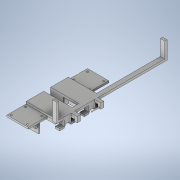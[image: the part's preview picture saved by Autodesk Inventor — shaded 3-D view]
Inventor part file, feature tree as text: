
AUTODESK INVENTOR PART (.ipt)
format: ipt  version: 2020.2 (Build 242310000, 310)  size: 848,896 bytes
history: native  units: mm
features: sketch x34, extrude x34, projected_geometry x17, hole x3
ambient origin geometry x8: Origin, YZ Plane, XZ Plane, XY Plane, X Axis, Y Axis, Z Axis, Center Point
bodies: Solid1 (feature_tree)
feature tree (88):
  sketch  "Sketch1"  dims[d0=8.0mm d1=98.298mm]
  extrude  "Extrusion1"  Depth=98.298mm
  extrude  "Extrusion2"  Depth=4.0mm
  extrude  "Extrusion3"  Depth=4.0mm TaperAngle=0.0deg
  extrude  "Extrusion4"  Depth=34.0mm
  extrude  "Extrusion5"  Depth=12.7mm
  extrude  "Extrusion6"  Depth=25.0mm
  hole  "Hole1"  [1 undecoded]
  extrude  "Extrusion11"  TaperAngle=60.0deg  [1 undecoded]
  extrude  "Extrusion12"  TaperAngle=120.0deg  [1 undecoded]
  sketch  "Sketch16"  dims[d19=6.4262mm d20=120.0deg]
  extrude  "Extrusion13"  Depth=6.4262mm
  extrude  "Extrusion14"  Depth=6.4262mm
  sketch  "Sketch17"  dims[d21=120.0deg d22=6.4262mm]
  extrude  "Extrusion15"  Depth=25.4mm TaperAngle=0.0deg
  extrude  "Extrusion18"  Depth=6.0mm
  extrude  "Extrusion19"  Depth=8.89mm
  extrude  "Extrusion20"  Depth=10.0mm
  hole  "Hole2"  [1 undecoded]
  extrude  "Extrusion21"  Depth=2.0mm
  extrude  "Extrusion22"  Depth=2.0mm
  sketch  "Sketch27"  dims[d45=8.89mm d46=2.0mm]
  extrude  "Extrusion23"  Depth=25.4mm
  extrude  "Extrusion24"  Depth=32.48mm
  extrude  "Extrusion25"  TaperAngle=90.0deg  [1 undecoded]
  sketch  "Sketch29"  dims[d79=51.53mm d80=32.48mm]
  extrude  "Extrusion26"  Depth=2.0mm
  extrude  "Extrusion27"  Depth=21.0mm
  extrude  "Extrusion28"  Depth=36.0mm TaperAngle=0.0deg
  extrude  "Extrusion29"  Depth=8.0mm
  extrude  "Extrusion30"  Depth=17.5mm
  extrude  "Extrusion32"  Depth=35.0mm
  extrude  "Extrusion38"  Depth=5.0mm
  extrude  "Extrusion39"  TaperAngle=90.0deg  [1 undecoded]
  extrude  "Extrusion40"  Depth=5.0mm
  hole  "Hole4"  [1 undecoded]
  extrude  "Extrusion43"  Depth=1.5mm
  extrude  "Extrusion44"  TaperAngle=0.0deg  [1 undecoded]
  extrude  "Extrusion45"  Depth=28.8036mm
  extrude  "Extrusion46"  Depth=25.4mm TaperAngle=0.0deg
  extrude  "Extrusion47"  Depth=2.0mm
  extrude  "Extrusion48"  Depth=2.0mm
  sketch  "Sketch2"  dims[d2=8.0mm d3=4.0mm]
  sketch  "Sketch3"  dims[d4=4.0mm d5=4.0mm d6=0.0mm]
  sketch  "Sketch4"  dims[d7=34.0mm d8=0.0mm d9=19.558mm]
  sketch  "Sketch5"  dims[d10=16.1125mm d11=12.7mm]
  sketch  "Sketch6"  dims[d12=25.0mm d13=0.0mm d14=11.1125mm]
  sketch  "Sketch14"  dims[d15=6.4135mm d16=12.827mm]
  projected_geometry  "Projected Loop2"
  sketch  "Sketch15"  dims[d17=6.4262mm d18=60.0deg]
  projected_geometry  "Projected Loop3"
  sketch  "Sketch18"  dims[d23=120.0deg d24=6.4262mm]
  sketch  "Sketch21"  dims[d25=120.0deg d26=25.4mm d27=0.0mm]
  sketch  "Sketch22"  dims[d28=6.0mm d29=8.89mm]
  sketch  "Sketch23"  dims[d30=5.9944mm d31=8.89mm]
  sketch  "Sketch24"  dims[d32=25.4mm d33=0.0mm d34=10.0mm]
  sketch  "Sketch25"  dims[d35=90.0deg d36=20.0mm]
  projected_geometry  "Projected Loop5"
  sketch  "Sketch26"  dims[d37=3.4mm d38=19.05mm d39=6.2992mm d40=6.35mm d41=90.0deg d42=5.0mm d43=0.0mm d44=2.0mm]
  sketch  "Sketch28"  dims[d47=25.4mm d48=0.0mm d78=16.24mm]
  sketch  "Sketch30"  dims[d81=90.0deg d82=90.0deg]
  sketch  "Sketch32"  dims[d83=4.0mm d84=0.0mm d87=2.0mm]
  projected_geometry  "Projected Loop6"
  sketch  "Sketch33"  dims[d88=2.0mm d89=21.0mm]
  projected_geometry  "Projected Loop7"
  sketch  "Sketch35"  dims[d90=2.0mm d91=36.0mm d92=0.0mm]
  projected_geometry  "Projected Loop8"
  sketch  "Sketch42"  dims[d93=13.878mm d94=8.0mm]
  sketch  "Sketch43"  dims[d95=180.0deg d96=17.5mm]
  projected_geometry  "Projected Loop9"
  projected_geometry  "Projected Loop10"
  projected_geometry  "Projected Loop11"
  projected_geometry  "Projected Loop12"
  sketch  "Sketch44"  dims[d97=90.0deg d98=35.0mm]
  sketch  "Sketch45"  dims[d99=3.5mm d100=5.0mm]
  sketch  "Sketch48"  dims[d101=7.0mm d102=90.0deg]
  sketch  "Sketch49"  dims[d103=5.0mm d104=3.4mm]
  projected_geometry  "Projected Loop13"
  projected_geometry  "Projected Loop14"
  sketch  "Sketch50"  dims[d105=3.4mm d106=25.4mm d107=0.0mm]
  projected_geometry  "Projected Loop15"
  sketch  "Sketch51"  dims[d108=6.4262mm d109=0.0mm d110=1.5mm]
  sketch  "Sketch52"  dims[d111=1.5mm d112=0.0mm d113=0.0mm]
  sketch  "Sketch53"  dims[d128=44.8mm d129=28.8036mm d130=25.4mm d131=0.0mm d132=3.2131mm d133=6.4262mm d134=120.0deg d135=3.2131mm d136=6.4262mm d137=120.0deg d138=25.4mm d139=0.0mm d140=8.001mm d141=13.8938mm d142=8.001mm d143=0.0mm d144=25.4mm d145=0.0mm d146=10.0mm d147=20.0mm d148=3.4mm d149=19.05mm d150=6.2992mm d151=6.35mm d152=90.0deg d153=5.0mm d154=0.0mm d155=16.2433mm d156=32.4866mm d157=51.5366mm d158=4.0mm d159=0.0mm d160=21.0mm d161=2.0mm d162=2.0mm d163=2.0mm d164=2.0mm d165=36.0mm d166=0.0mm d167=7.0mm d168=5.0mm d169=5.0mm d170=17.5mm d171=35.0mm d172=3.4mm d173=3.4mm d174=5.0mm d175=0.0mm d176=5.0mm d177=0.0mm d178=1.5mm d179=1.5mm d180=25.4mm d181=0.0mm d182=19.05mm d183=10.0mm d184=5.08mm d185=4.0mm d186=0.0mm d187=10.0mm d188=0.0mm d189=2.0mm d190=2.0mm d191=25.4mm d192=0.0mm d194=30.0mm d195=0.0mm d196=99.06mm d197=0.0mm d201=11.43mm d202=0.0mm d239=25.4mm d240=0.0mm d241=1.5mm d242=0.0mm d243=39.0mm d244=35.0mm d245=39.0mm d246=35.0mm d247=3.0mm d248=0.0mm d249=5.0mm d250=5.0mm d251=29.7mm d252=26.05mm d253=4.0mm d254=4.0mm d255=29.7mm d256=26.05mm d257=3.4mm d258=19.05mm d259=6.2992mm d260=6.35mm d261=90.0deg d262=25.4mm d263=20.594885mm d271=4.0mm d272=28.4mm d273=0.0mm d274=25.4mm d275=0.0mm d276=3.429mm d277=180.0deg d278=30.0mm d279=0.0mm d280=6.35mm d281=25.4mm d282=0.0mm d283=5.08mm d284=25.4mm d285=0.0mm d286=2.0mm d287=0.0mm d214=12.7mm d215=0.872665mm d216=12.7mm d217=0.872665mm d228=12.7mm d229=0.872665mm d230=12.7mm d231=0.872665mm]
  projected_geometry  "Projected Loop16"
  projected_geometry  "Projected Loop17"
  projected_geometry  "Projected Loop18"
  projected_geometry  "Projected Loop19"
note: 8 required parameter values undecoded (feature->parameter linkage not recoverable at this tier; creation-order binding heuristic only, values carry confidence <= 0.55)
